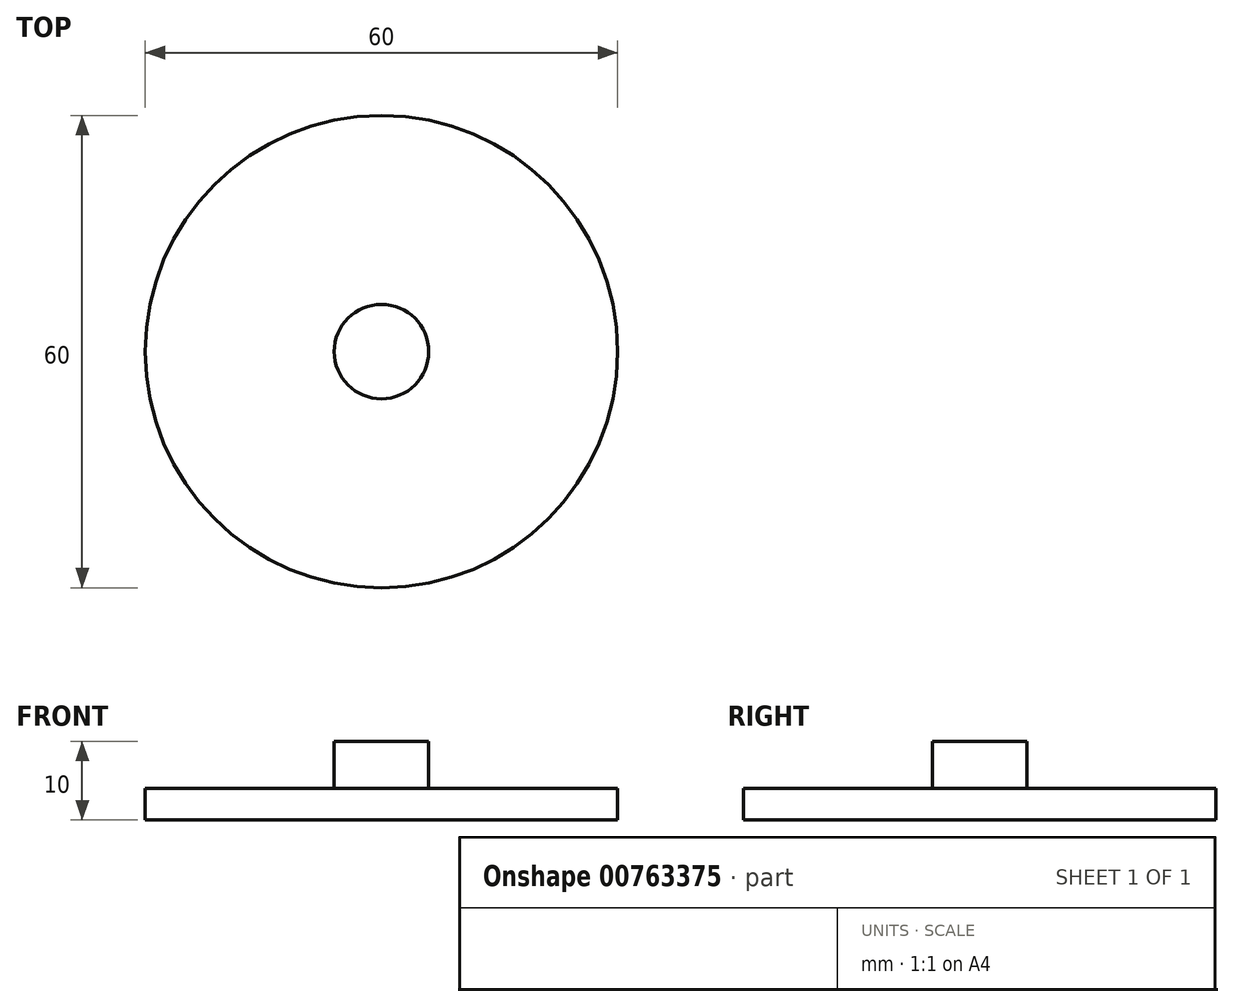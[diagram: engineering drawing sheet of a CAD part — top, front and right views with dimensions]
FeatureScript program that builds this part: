
annotation { "Feature Type Name" : "Feature", "Feature Type Description" : "" }
export const myFeature = defineFeature(function(context is Context, id is Id, definition is map)
    precondition{}
    {
        {
            var Q0;
            Q0=qCreatedBy(makeId("Top.planeOp"),FACE);
            var sketch = newSketch(context, id + "F0", { "sketchPlane" : qUnion([Q0])});
            skCircle(sketch, "E0", {"center": v(0, 0) * mm, "radius": 30 * mm});
            skCircle(sketch, "E1", {"center": v(0, 0) * mm, "radius": 6 * mm});
            skSolve(sketch);
        }
        {
            var Q0;
            Q0=makeQuery(id+"F0.imprint","IMPRINT",FACE,{"disambiguationData":[TD([[makeQuery(id+"F0.imprint","IMPRINT",EDGE,{"derivedFrom":sQuery(id+"F0.wireOp",EDGE,"E0")}),1.0]])]});
            var Q1;
            Q1=makeQuery(id+"F0.imprint","IMPRINT",FACE,{"disambiguationData":[TD([[makeQuery(id+"F0.imprint","IMPRINT",EDGE,{"derivedFrom":sQuery(id+"F0.wireOp",EDGE,"E1")}),1.0]])]});
            extrude(context, id + "F1", {"entities" : qUnion([Q0, Q1]), "oppositeDirection" : true, "depth" : 4 * mm, "offsetDistance" : 25 * mm});
        }
        {
            var Q0;
            Q0=makeQuery(id+"F0.imprint","IMPRINT",FACE,{"disambiguationData":[TD([[makeQuery(id+"F0.imprint","IMPRINT",EDGE,{"derivedFrom":sQuery(id+"F0.wireOp",EDGE,"E1")}),1.0]])]});
            var Q1;
            Q1=sQuery(id+"F0.wireOp",EDGE,"E1");
            extrude(context, id + "F2", {"entities" : qUnion([Q0]), "operationType" : NewBodyOperationType.ADD, "surfaceEntities" : qUnion([Q1]), "depth" : 6 * mm, "offsetDistance" : 25 * mm});
        }
    });
